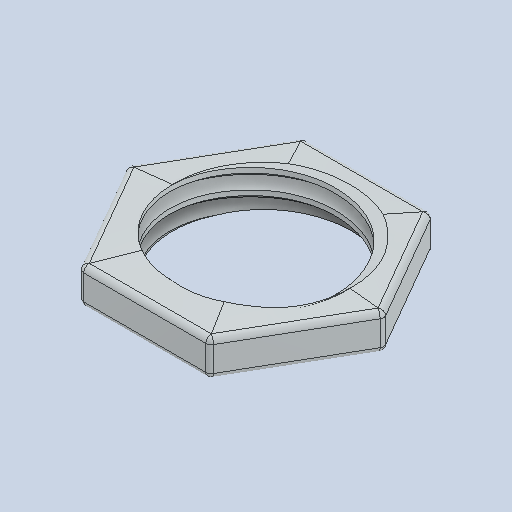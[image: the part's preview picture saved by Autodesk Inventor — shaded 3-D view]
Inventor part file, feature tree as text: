
AUTODESK INVENTOR PART (.ipt)
format: ipt  version: 2025.1 (Build 291241020, 241B)  size: 276,480 bytes
history: native  units: in
note: dims shown in document units (in); Inventor stores cm internally (conversion verified against a paired STEP export)
features: other x3, thread x1
ambient origin geometry x8: Origin, YZ Plane, XZ Plane, XY Plane, X Axis, Y Axis, Z Axis, Center Point
bodies: Solid1 (feature_tree)
feature tree (4):
  other  "Plane1"
  other  "Plane2"
  other  "Plane3"
  thread  "Thread1"  [1 undecoded]
note: 1 required parameter value undecoded (feature->parameter linkage not recoverable at this tier; creation-order binding heuristic only, values carry confidence <= 0.55)
